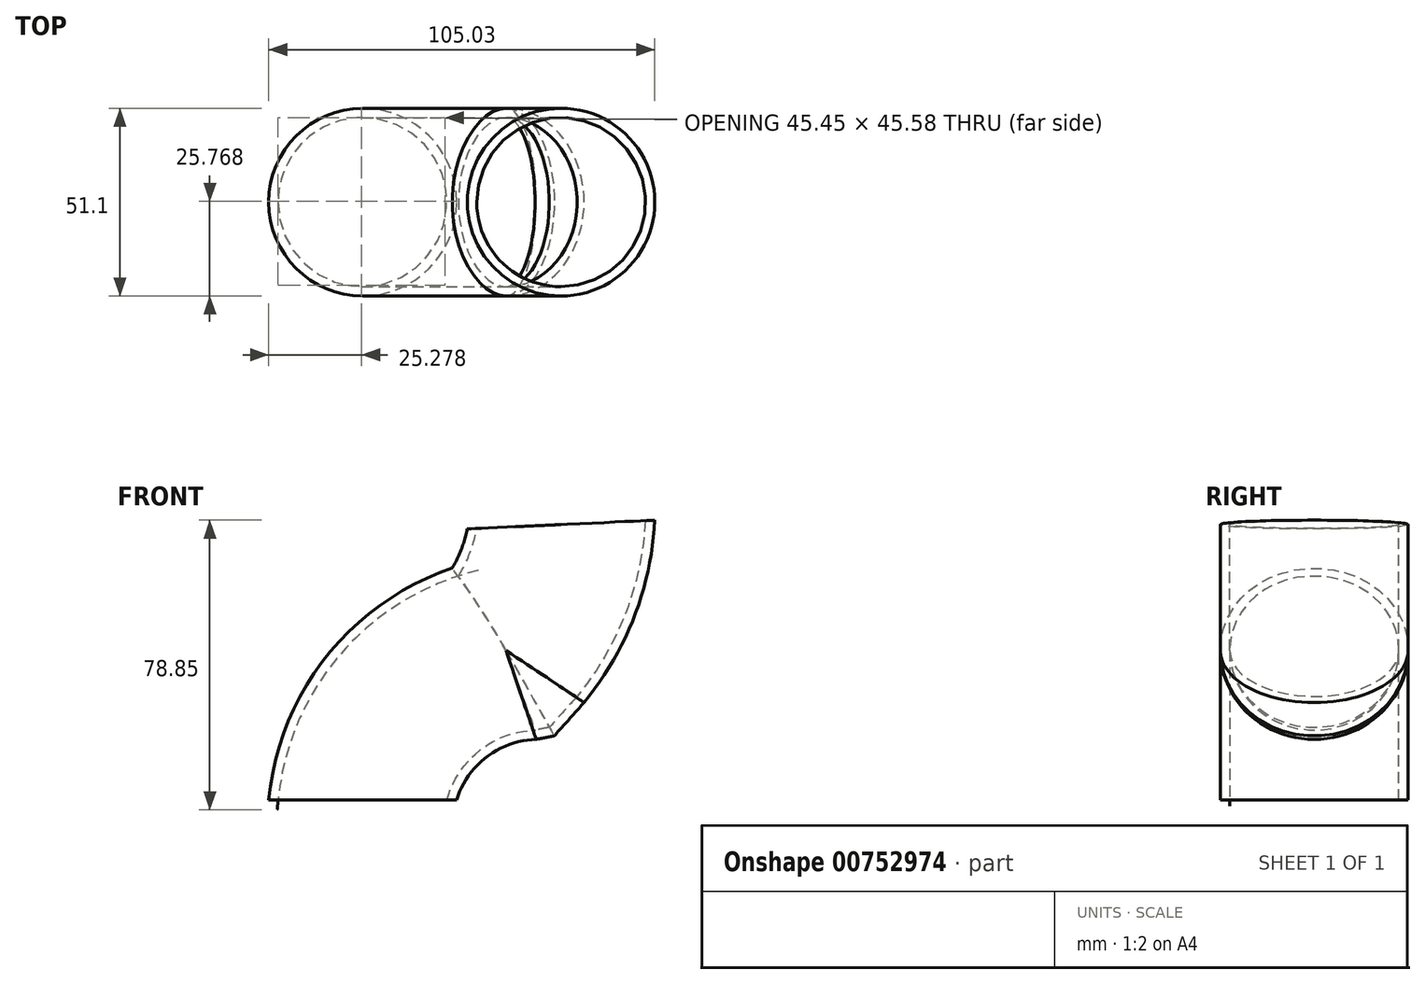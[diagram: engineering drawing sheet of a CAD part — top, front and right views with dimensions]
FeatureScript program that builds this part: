
annotation { "Feature Type Name" : "Feature", "Feature Type Description" : "" }
export const myFeature = defineFeature(function(context is Context, id is Id, definition is map)
    precondition{}
    {
        {
            var Q0;
            Q0=qCreatedBy(makeId("Top.planeOp"),FACE);
            var sketch = newSketch(context, id + "F0", { "sketchPlane" : qUnion([Q0])});
            skCircle(sketch, "E0", {"center": v(0, 0) * mm, "radius": 25.55 * mm});
            skSolve(sketch);
        }
        {
            var Q0;
            Q0=qCreatedBy(makeId("Front.planeOp"),FACE);
            var sketch = newSketch(context, id + "F1", { "sketchPlane" : qUnion([Q0])});
            skArc(sketch, "E1", {"start": v(39, 40.72) * mm, "mid": v(12.95, 26.63) * mm, "end": v(0, 0) * mm});
            skArc(sketch, "E2", {"start": v(39, 40.72) * mm, "mid": v(49.22, 56.65) * mm, "end": v(53.96, 74.97) * mm});
            skSolve(sketch);
        }
        {
            var Q0;
            Q0=makeQuery(id+"F0.imprint","IMPRINT",FACE,{"disambiguationData":[TD([[makeQuery(id+"F0.imprint","IMPRINT",EDGE,{"derivedFrom":sQuery(id+"F0.wireOp",EDGE,"E0")}),1.0]])]});
            var Q1;
            Q1=sQuery(id+"F1.wireOp",EDGE,"E1");
            var Q2;
            Q2=sQuery(id+"F1.wireOp",EDGE,"E2");
            sweep(context, id + "F2", {"profiles" : qUnion([Q0]), "path" : qUnion([Q1, Q2])});
        }
        {
            var Q0;
            Q0=makeQuery(id+"F2.opSweep","CAP_FACE",FACE,{"disambiguationData":[OSD([sQuery(id+"F0.wireOp",EDGE,"E0"),sQuery(id+"F1.wireOp",VERTEX,"E2.end")])],"isStart":false});
            var Q1;
            Q1=makeQuery(id+"F2.opSweep","CAP_FACE",FACE,{"disambiguationData":[OSD([sQuery(id+"F0.wireOp",EDGE,"E0"),sQuery(id+"F1.wireOp",VERTEX,"E1.end")])],"isStart":true});
            shell(context, id + "F3", {"entities" : qUnion([Q0, Q1]), "thickness" : 2.54 * mm});
        }
    });
